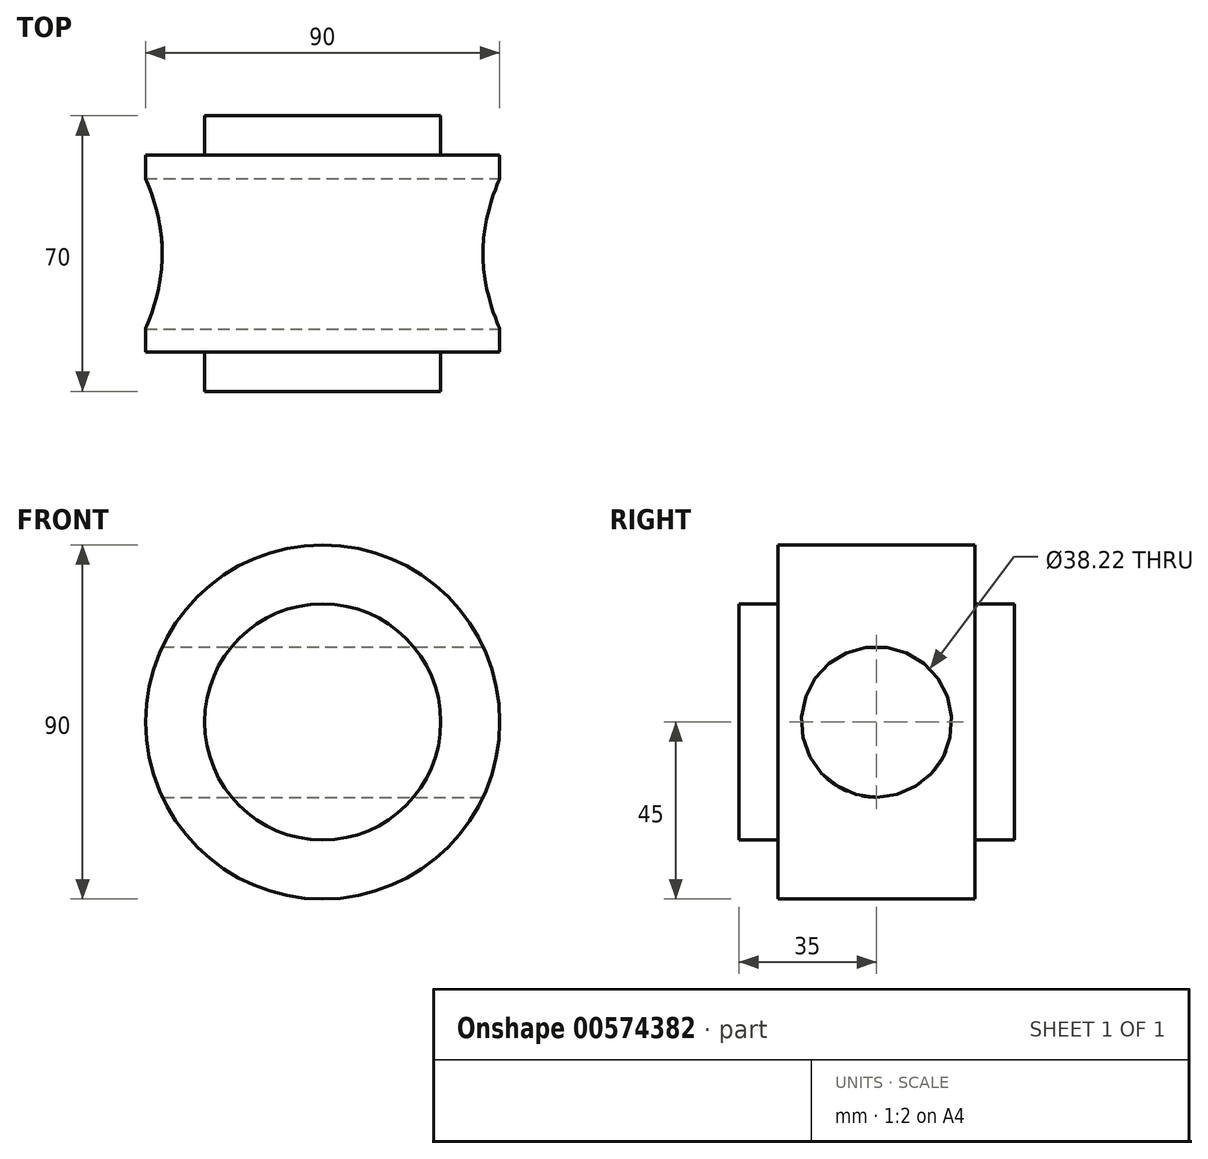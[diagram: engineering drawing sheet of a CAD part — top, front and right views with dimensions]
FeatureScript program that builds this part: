
annotation { "Feature Type Name" : "Feature", "Feature Type Description" : "" }
export const myFeature = defineFeature(function(context is Context, id is Id, definition is map)
    precondition{}
    {
        {
            var Q0;
            Q0=qCreatedBy(makeId("Front.planeOp"),FACE);
            var sketch = newSketch(context, id + "F0", { "sketchPlane" : qUnion([Q0])});
            skCircle(sketch, "E0", {"center": v(0, 0) * mm, "radius": 30 * mm});
            skCircle(sketch, "E1", {"center": v(0, 0) * mm, "radius": 45 * mm});
            skSolve(sketch);
        }
        {
            var Q0;
            Q0=makeQuery(id+"F0.imprint","IMPRINT",FACE,{"disambiguationData":[TD([[makeQuery(id+"F0.imprint","IMPRINT",EDGE,{"derivedFrom":sQuery(id+"F0.wireOp",EDGE,"E0")}),1.0]])]});
            extrude(context, id + "F1", {"entities" : qUnion([Q0]), "endBound" : BoundingType.SYMMETRIC, "depth" : 70 * mm, "offsetDistance" : 25 * mm});
        }
        {
            var Q0;
            Q0 = qSketchRegion(id + "F0", true);
            extrude(context, id + "F2", {"entities" : qUnion([Q0]), "operationType" : NewBodyOperationType.ADD, "endBound" : BoundingType.SYMMETRIC, "depth" : 50 * mm, "offsetDistance" : 25 * mm});
        }
        {
            var Q0;
            Q0=qCreatedBy(makeId("Right.planeOp"),FACE);
            var sketch = newSketch(context, id + "F3", { "sketchPlane" : qUnion([Q0])});
            skCircle(sketch, "E2", {"center": v(0, 0) * mm, "radius": 19.11 * mm});
            skSolve(sketch);
        }
        {
            var Q0;
            Q0 = qSketchRegion(id + "F3", true);
            extrude(context, id + "F4", {"entities" : qUnion([Q0]), "operationType" : NewBodyOperationType.REMOVE, "endBound" : BoundingType.SYMMETRIC, "oppositeDirection" : true, "depth" : 90 * mm, "offsetDistance" : 25 * mm});
        }
    });
